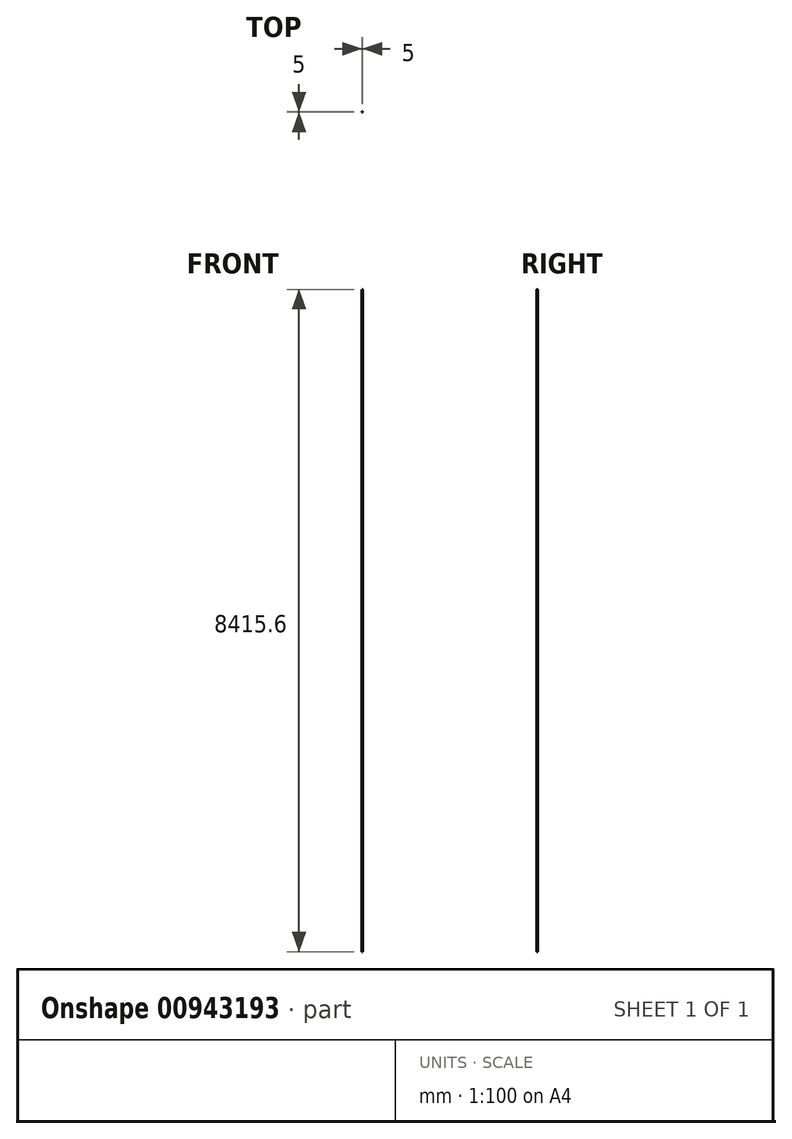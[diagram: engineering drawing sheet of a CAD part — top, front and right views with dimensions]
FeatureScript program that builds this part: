
annotation { "Feature Type Name" : "Feature", "Feature Type Description" : "" }
export const myFeature = defineFeature(function(context is Context, id is Id, definition is map)
    precondition{}
    {
        {
            var Q0;
            Q0=qCreatedBy(makeId("Top.planeOp"),FACE);
            var sketch = newSketch(context, id + "F0", { "sketchPlane" : qUnion([Q0])});
            skCircle(sketch, "E0", {"center": v(0, 0) * mm, "radius": 2.5 * mm});
            skSolve(sketch);
        }
        {
            var Q0;
            Q0=qSketchRegion(id+"F0",true);
            extrude(context, id + "F1", {"entities" : qUnion([Q0]), "depth" : 8415.6 * mm, "offsetDistance" : 25 * mm});
        }
    });
